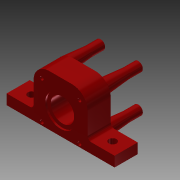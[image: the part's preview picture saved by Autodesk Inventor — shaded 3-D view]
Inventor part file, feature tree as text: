
AUTODESK INVENTOR PART (.ipt)
format: ipt  version: 2014 (Build 180170000, 170)  size: 216,576 bytes
history: native  units: in
note: dims shown in document units (in); Inventor stores cm internally (conversion verified against a paired STEP export)
features: extrude x7, sketch x7, reference x4, fillet x2, plane x2, projected_geometry x1
ambient origin geometry x8: Origin, YZ Plane, XZ Plane, XY Plane, X Axis, Y Axis, Z Axis, Center Point
bodies: Solid1 (feature_tree)
feature tree (23):
  extrude  "Extrusion1"  Depth=3.5in
  extrude  "Extrusion2"  Depth=0.75in TaperAngle=0.0deg
  fillet  "Fillet1"  Radius=0.25in
  extrude  "Extrusion3"  Depth=0.125in
  extrude  "Extrusion4"  Depth=0.06in TaperAngle=0.0deg
  sketch  "Sketch5"  dims[d16=1.75in d17=1.65in d18=0.7095in]
  plane  "Work Plane1"
  extrude  "Extrusion5"  Depth=1.65in
  fillet  "Fillet2"  Radius=0.7095in
  plane  "Work Plane2"
  extrude  "Extrusion7"  Depth=0.3in
  extrude  "Extrusion8"  Depth=0.5in
  sketch  "Sketch1"  dims[d0=0.759in d1=3.5in]
  sketch  "Sketch2"  dims[d3=0.33in d6=0.75in d7=0.0in d8=0.25in]
  projected_geometry  "Projected Loop1"
  sketch  "Sketch3"  dims[d9=0.66in d10=0.0in d11=0.125in]
  sketch  "Sketch4"  dims[d12=1.0in d13=0.06in d14=0.0in]
  reference  "Reference1"
  reference  "Reference2"
  reference  "Reference3"
  reference  "Reference4"
  sketch  "Sketch8"  dims[d19=1.0in d20=0.0in d21=0.3in]
  sketch  "Sketch9"  dims[d22=1.0in d23=0.0in d26=0.5in d27=0.75in d28=1.0in d29=0.0344in d30=1.0in d31=0.0in]
